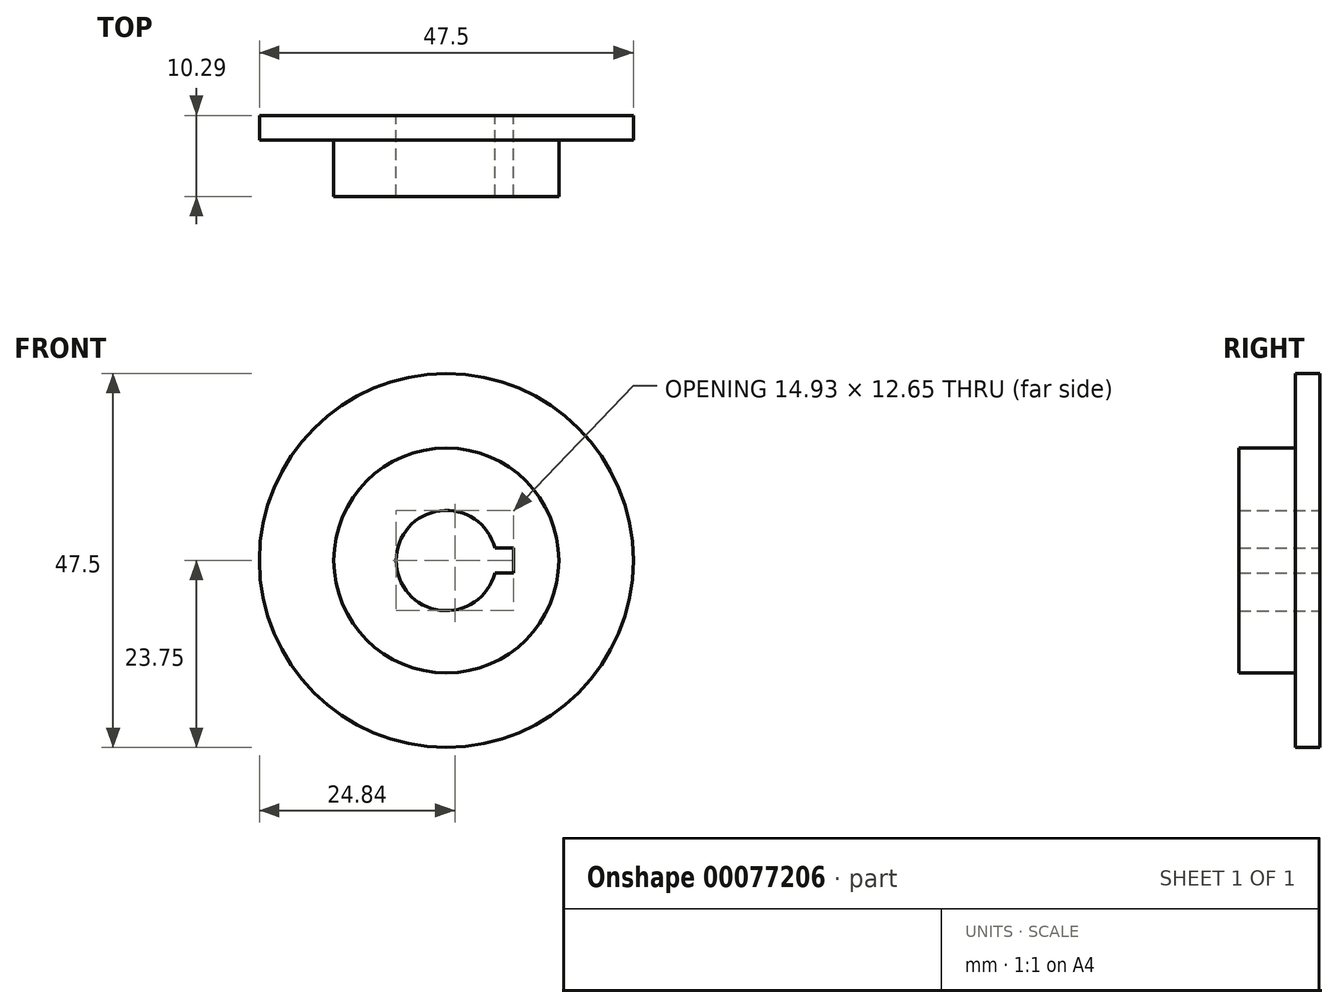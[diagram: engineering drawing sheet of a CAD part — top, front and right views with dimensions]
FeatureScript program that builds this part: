
annotation { "Feature Type Name" : "Feature", "Feature Type Description" : "" }
export const myFeature = defineFeature(function(context is Context, id is Id, definition is map)
    precondition{}
    {
        {
            var Q0;
            Q0=qCreatedBy(makeId("Front.planeOp"),FACE);
            var sketch = newSketch(context, id + "F0", { "sketchPlane" : qUnion([Q0])});
            skCircle(sketch, "E0", {"center": v(0, 0) * mm, "radius": 23.75 * mm});
            skArc(sketch, "E1", {"start": v(6.17, 1.59) * mm, "mid": v(-6.38, 0) * mm, "end": v(6.17, -1.59) * mm});
            skLineSegment(sketch, "E2", {"start": v(6.17, -1.59) * mm, "end": v(8.56, -1.59) * mm});
            skLineSegment(sketch, "E3", {"start": v(8.56, -1.59) * mm, "end": v(8.56, 1.59) * mm});
            skLineSegment(sketch, "E4", {"start": v(8.56, 1.59) * mm, "end": v(6.17, 1.59) * mm});
            skSolve(sketch);
        }
        {
            var Q0;
            Q0=makeQuery(id+"F0.imprint","IMPRINT",FACE,{"disambiguationData":[TD([[makeQuery(id+"F0.imprint","IMPRINT",EDGE,{"derivedFrom":sQuery(id+"F0.wireOp",EDGE,"E0")}),1.0]])]});
            extrude(context, id + "F1", {"entities" : qUnion([Q0]), "depth" : 3.12 * mm});
        }
        {
            var Q0;
            Q0=makeQuery(id+"F1.opExtrude","CAP_FACE",FACE,{"disambiguationData":[OSD([sQuery(id+"F0.wireOp",EDGE,"E0"),sQuery(id+"F0.wireOp",EDGE,"E1"),sQuery(id+"F0.wireOp",EDGE,"E2"),sQuery(id+"F0.wireOp",EDGE,"E3"),sQuery(id+"F0.wireOp",EDGE,"E4")])],"isStart":false});
            var sketch = newSketch(context, id + "F2", { "sketchPlane" : qUnion([Q0])});
            skCircle(sketch, "E5", {"center": v(0, 0) * mm, "radius": 14.29 * mm});
            skSolve(sketch);
        }
        {
            var Q0;
            Q0=makeQuery(id+"F2.imprint","IMPRINT",FACE,{"disambiguationData":[TD([[makeQuery(id+"F2.imprint","IMPRINT",EDGE,{"derivedFrom":sQuery(id+"F2.wireOp",EDGE,"E5")}),1.0]])]});
            extrude(context, id + "F3", {"entities" : qUnion([Q0]), "operationType" : NewBodyOperationType.ADD, "depth" : 7.16 * mm});
        }
    });
